# Revit family: Barrier_Gate_AutoGate_Catawba
name_source: partatom
category: Generic Models
revit_build: Autodesk Revit 2015 (Build: 20140606_1530(x64)
units: mm (PartAtom-declared; Revit-internal decimal feet)

## types (4) — shared parameters
Assembly Code = E1030900
Concave = No
Construction Details = http://www.arcat.com
Convex = Yes
Default Elevation = 0' - 0"
Include Finials = Yes
Keynote = 32 21 00
Manufacturer = AutoGate, Inc
Manufacturer Fax = 419-588-3514
Manufacturer Website = http://autogate.com
Maximum Size = 25 x 8 ft (W x H)
Number of Interior Design Repeats = 36
Product Data = http://www.arcat.com
Revision = R1_2016-11
Sales Information = http://autogate.com
Specification = http://www.arcat.com
URL = http://autogate.com
zero-valued in all types: Expected Lifespan (Years), Maintenance Schedule (Months), Warranty Duration (Years)

## per-type parameters (varying)
| type | Description | Model |
| Size as Specified Convex | AutoGate Catawba Convex Gate as Specified | Catawba 400 Convex |
| Size as Specified Convex with Finials | AutoGate Catawba Convex Gate as Specified | Catawba 400 Convex with Finials |
| Size as Specified Concave | AutoGate Catawba Concave Gate as Specified | Catawba 400 Concave |
| Size as Specified Concave with Finials | AutoGate Catawba Concave Gate as Specified | Catawba 400 Concave with Finials |

## geometry (parser evidence)
native form markers: Sweep x4
no freeform markers — native parametric forms only
